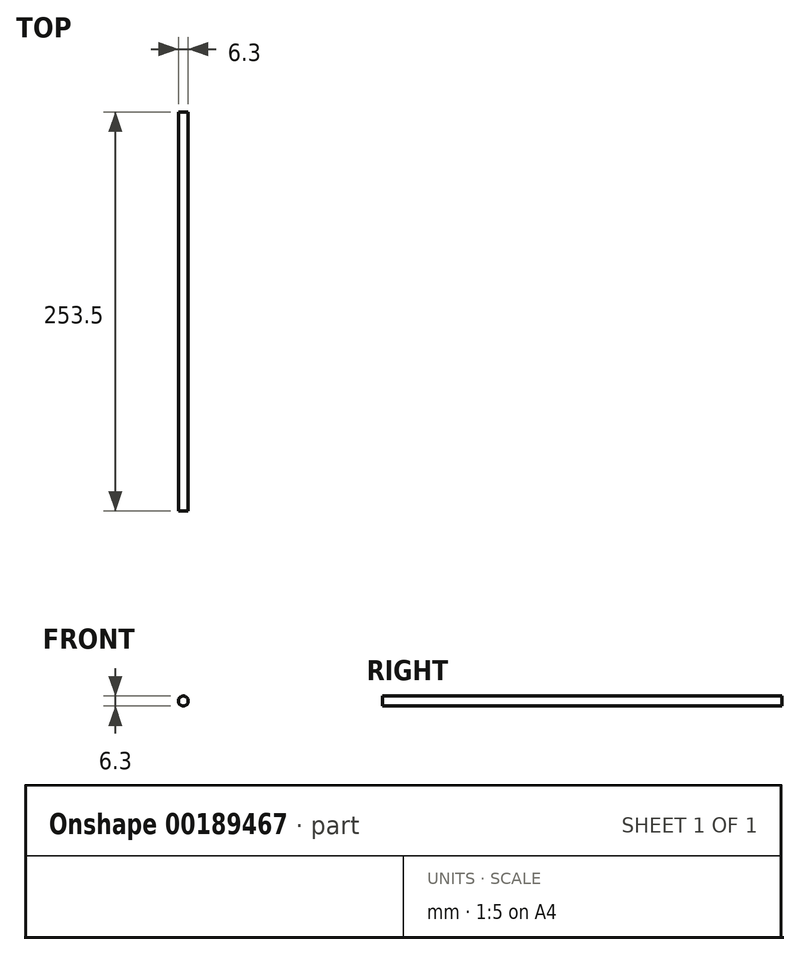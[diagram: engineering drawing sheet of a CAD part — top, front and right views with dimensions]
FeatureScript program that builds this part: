
annotation { "Feature Type Name" : "Feature", "Feature Type Description" : "" }
export const myFeature = defineFeature(function(context is Context, id is Id, definition is map)
    precondition{}
    {
        {
            var Q0;
            Q0=qCreatedBy(makeId("Front.planeOp"),FACE);
            var sketch = newSketch(context, id + "F0", { "sketchPlane" : qUnion([Q0])});
            skCircle(sketch, "E0", {"center": v(0, 0) * mm, "radius": 3.15 * mm});
            skSolve(sketch);
        }
        {
            var Q0;
            Q0=makeQuery(id+"F0.imprint","IMPRINT",FACE,{"disambiguationData":[TD([[makeQuery(id+"F0.imprint","IMPRINT",EDGE,{"derivedFrom":sQuery(id+"F0.wireOp",EDGE,"E0")}),1.0]])]});
            extrude(context, id + "F1", {"entities" : qUnion([Q0]), "depth" : 253.5 * mm});
        }
    });
